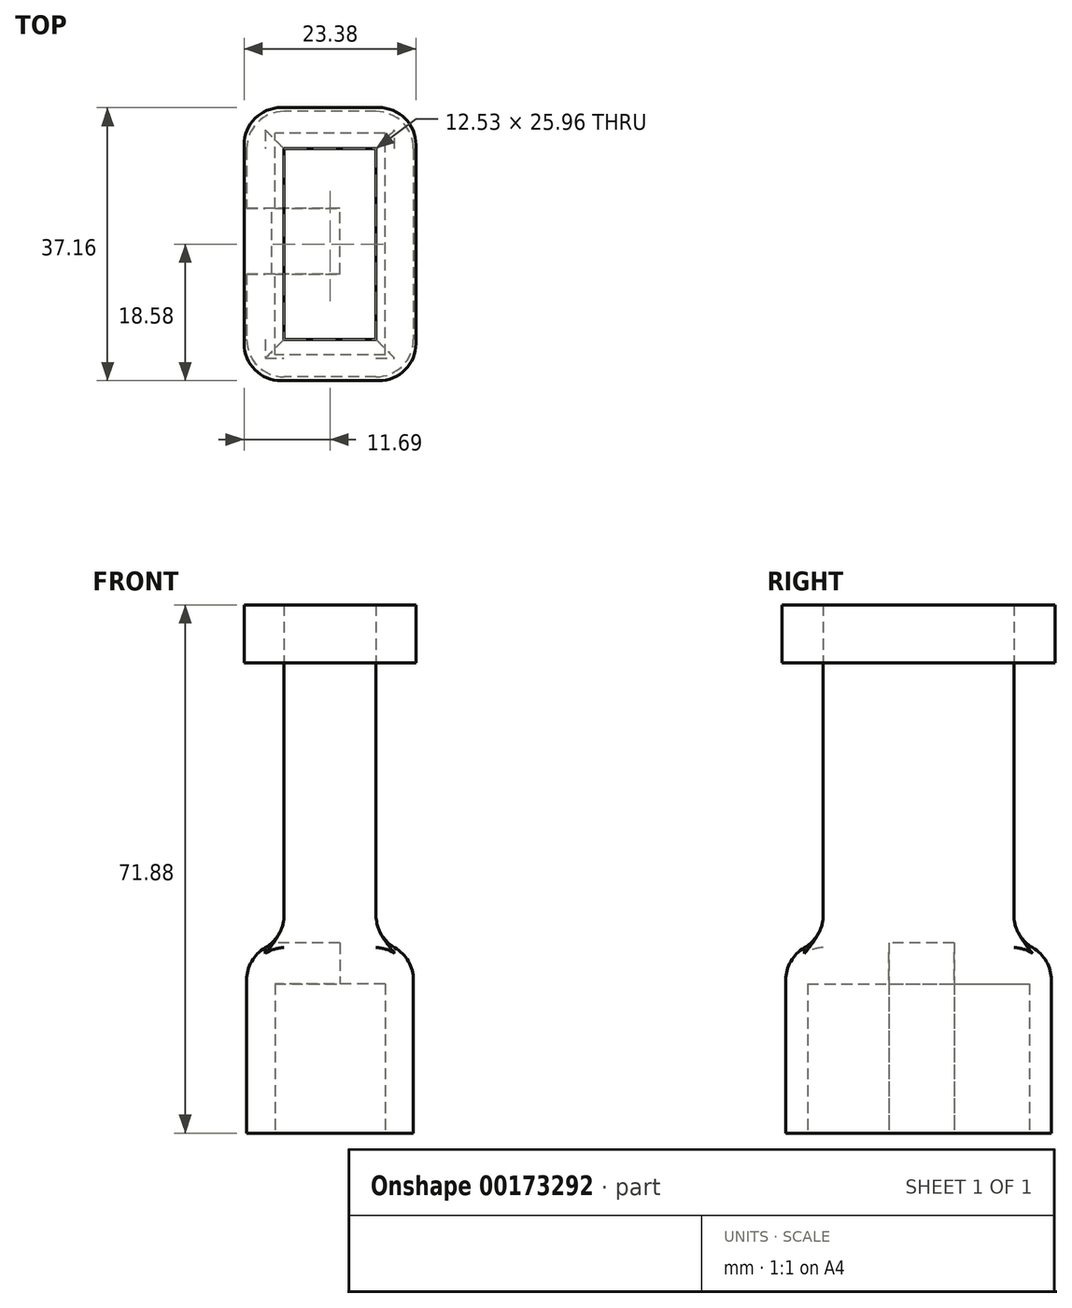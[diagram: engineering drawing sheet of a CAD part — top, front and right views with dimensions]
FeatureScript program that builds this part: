
annotation { "Feature Type Name" : "Feature", "Feature Type Description" : "" }
export const myFeature = defineFeature(function(context is Context, id is Id, definition is map)
    precondition{}
    {
        {
            var Q0;
            Q0=qCreatedBy(makeId("Top.planeOp"),FACE);
            var sketch = newSketch(context, id + "F0", { "sketchPlane" : qUnion([Q0])});
            skLineSegment(sketch, "E0.bottom", {"start": v(11.34, 18.06) * mm, "end": v(-11.34, 18.06) * mm});
            skLineSegment(sketch, "E0.top", {"start": v(11.34, -18.06) * mm, "end": v(-11.34, -18.06) * mm});
            skLineSegment(sketch, "E0.left", {"start": v(11.34, 18.06) * mm, "end": v(11.34, -18.06) * mm});
            skLineSegment(sketch, "E0.right", {"start": v(-11.34, 18.06) * mm, "end": v(-11.34, -18.06) * mm});
            skPoint(sketch, "E0.middle", {"position": v(0, 0) * mm});
            skSolve(sketch);
        }
        {
            var Q0;
            Q0=makeQuery(id+"F0.imprint","IMPRINT",FACE,{"disambiguationData":[TD([[makeQuery(id+"F0.imprint","IMPRINT",EDGE,{"derivedFrom":sQuery(id+"F0.wireOp",EDGE,"E0.bottom")}),1.0]])]});
            extrude(context, id + "F1", {"entities" : qUnion([Q0]), "depth" : 25.9 * mm});
        }
        {
            var Q0;
            Q0=makeQuery(id+"F1.opExtrude","CAP_EDGE",EDGE,{"disambiguationData":[OSD([sQuery(id+"F0.wireOp",EDGE,"E0.right")])],"isStart":false});
            var Q1;
            Q1=makeQuery(id+"F1.opExtrude","CAP_EDGE",EDGE,{"disambiguationData":[OSD([sQuery(id+"F0.wireOp",EDGE,"E0.bottom")])],"isStart":false});
            var Q2;
            Q2=makeQuery(id+"F1.opExtrude","SWEPT_EDGE",EDGE,{"disambiguationData":[OSD([sQuery(id+"F0.wireOp",EDGE,"E0.bottom"),sQuery(id+"F0.wireOp",EDGE,"E0.right")])]});
            var Q3;
            Q3=makeQuery(id+"F1.opExtrude","SWEPT_EDGE",EDGE,{"disambiguationData":[OSD([sQuery(id+"F0.wireOp",EDGE,"E0.bottom"),sQuery(id+"F0.wireOp",EDGE,"E0.left")])]});
            var Q4;
            Q4=makeQuery(id+"F1.opExtrude","CAP_EDGE",EDGE,{"disambiguationData":[OSD([sQuery(id+"F0.wireOp",EDGE,"E0.left")])],"isStart":false});
            var Q5;
            Q5=makeQuery(id+"F1.opExtrude","CAP_EDGE",EDGE,{"disambiguationData":[OSD([sQuery(id+"F0.wireOp",EDGE,"E0.top")])],"isStart":false});
            var Q6;
            Q6=makeQuery(id+"F1.opExtrude","SWEPT_EDGE",EDGE,{"disambiguationData":[OSD([sQuery(id+"F0.wireOp",EDGE,"E0.top"),sQuery(id+"F0.wireOp",EDGE,"E0.left")])]});
            var Q7;
            Q7=makeQuery(id+"F1.opExtrude","SWEPT_EDGE",EDGE,{"disambiguationData":[OSD([sQuery(id+"F0.wireOp",EDGE,"E0.top"),sQuery(id+"F0.wireOp",EDGE,"E0.right")])]});
            fillet(context, id + "F2", {"entities" : qUnion([Q0, Q1, Q2, Q3, Q4, Q5, Q6, Q7]), "radius" : 5.08 * mm, "tangentPropagation" : true, "allowEdgeOverflow" : false});
        }
        {
            var Q0;
            Q0=makeQuery(id+"F1.opExtrude","CAP_FACE",FACE,{"disambiguationData":[OSD([sQuery(id+"F0.wireOp",EDGE,"E0.bottom"),sQuery(id+"F0.wireOp",EDGE,"E0.top"),sQuery(id+"F0.wireOp",EDGE,"E0.left"),sQuery(id+"F0.wireOp",EDGE,"E0.right")])],"isStart":false});
            var sketch = newSketch(context, id + "F3", { "sketchPlane" : qUnion([Q0])});
            skLineSegment(sketch, "E1.bottom", {"start": v(6.26, 12.98) * mm, "end": v(-6.26, 12.98) * mm});
            skLineSegment(sketch, "E1.top", {"start": v(6.26, -12.98) * mm, "end": v(-6.26, -12.98) * mm});
            skLineSegment(sketch, "E1.left", {"start": v(6.26, 12.98) * mm, "end": v(6.26, -12.98) * mm});
            skLineSegment(sketch, "E1.right", {"start": v(-6.26, 12.98) * mm, "end": v(-6.26, -12.98) * mm});
            skPoint(sketch, "E1.middle", {"position": v(0, 0) * mm});
            skSolve(sketch);
        }
        {
            var Q0;
            Q0=makeQuery(id+"F3.imprint","IMPRINT",FACE,{"disambiguationData":[TD([[makeQuery(id+"F3.imprint","IMPRINT",EDGE,{"derivedFrom":sQuery(id+"F3.wireOp",EDGE,"E1.bottom")}),1.0]])]});
            extrude(context, id + "F4", {"entities" : qUnion([Q0]), "operationType" : NewBodyOperationType.ADD, "depth" : 38.1 * mm});
        }
        {
            var Q0;
            Q0=makeQuery(id+"F4.opExtrude","CAP_FACE",FACE,{"disambiguationData":[OSD([sQuery(id+"F3.wireOp",EDGE,"E1.bottom"),sQuery(id+"F3.wireOp",EDGE,"E1.top"),sQuery(id+"F3.wireOp",EDGE,"E1.left"),sQuery(id+"F3.wireOp",EDGE,"E1.right")])],"isStart":false});
            var sketch = newSketch(context, id + "F5", { "sketchPlane" : qUnion([Q0])});
            skLineSegment(sketch, "E2.bottom", {"start": v(11.7, 18.58) * mm, "end": v(-11.7, 18.58) * mm});
            skLineSegment(sketch, "E2.top", {"start": v(11.7, -18.58) * mm, "end": v(-11.7, -18.58) * mm});
            skLineSegment(sketch, "E2.left", {"start": v(11.7, 18.58) * mm, "end": v(11.7, -18.58) * mm});
            skLineSegment(sketch, "E2.right", {"start": v(-11.7, 18.58) * mm, "end": v(-11.7, -18.58) * mm});
            skPoint(sketch, "E2.middle", {"position": v(0, 0) * mm});
            skSolve(sketch);
        }
        {
            var Q0;
            Q0=makeQuery(id+"F5.imprint","IMPRINT",FACE,{"disambiguationData":[TD([[makeQuery(id+"F5.imprint","IMPRINT",EDGE,{"derivedFrom":sQuery(id+"F5.wireOp",EDGE,"E2.bottom")}),1.0]])]});
            extrude(context, id + "F6", {"entities" : qUnion([Q0]), "depth" : 7.87 * mm});
        }
        {
            var Q0;
            Q0=makeQuery(id+"F4.opExtrude","CAP_FACE",FACE,{"disambiguationData":[OSD([sQuery(id+"F3.wireOp",EDGE,"E1.bottom"),sQuery(id+"F3.wireOp",EDGE,"E1.top"),sQuery(id+"F3.wireOp",EDGE,"E1.left"),sQuery(id+"F3.wireOp",EDGE,"E1.right")])],"isStart":false});
            var Q1;
            Q1=makeQuery(id+"F6.opExtrude","CAP_FACE",FACE,{"disambiguationData":[OSD([sQuery(id+"F3.wireOp",EDGE,"E1.bottom"),sQuery(id+"F3.wireOp",EDGE,"E1.top"),sQuery(id+"F3.wireOp",EDGE,"E1.left"),sQuery(id+"F3.wireOp",EDGE,"E1.right"),sQuery(id+"F5.wireOp",EDGE,"E2.bottom"),sQuery(id+"F5.wireOp",EDGE,"E2.top"),sQuery(id+"F5.wireOp",EDGE,"E2.left"),sQuery(id+"F5.wireOp",EDGE,"E2.right")])],"isStart":false});
            extrude(context, id + "F7", {"entities" : qUnion([Q0]), "endBound" : BoundingType.UP_TO_SURFACE, "endBoundEntityFace" : qUnion([Q1]), "depth" : 7.37 * mm});
        }
        {
            var Q0;
            Q0=makeQuery(id+"F1.opExtrude","CAP_FACE",FACE,{"disambiguationData":[OSD([sQuery(id+"F0.wireOp",EDGE,"E0.bottom"),sQuery(id+"F0.wireOp",EDGE,"E0.top"),sQuery(id+"F0.wireOp",EDGE,"E0.left"),sQuery(id+"F0.wireOp",EDGE,"E0.right")])],"isStart":true});
            var sketch = newSketch(context, id + "F8", { "sketchPlane" : qUnion([Q0])});
            skLineSegment(sketch, "E3.bottom", {"start": v(7.5, 15.1) * mm, "end": v(-7.5, 15.1) * mm});
            skLineSegment(sketch, "E3.top", {"start": v(7.5, -15.1) * mm, "end": v(-7.5, -15.1) * mm});
            skLineSegment(sketch, "E3.left", {"start": v(7.5, 15.1) * mm, "end": v(7.5, -15.1) * mm});
            skLineSegment(sketch, "E3.right", {"start": v(-7.5, 15.1) * mm, "end": v(-7.5, -15.1) * mm});
            skPoint(sketch, "E3.middle", {"position": v(0, 0) * mm});
            skSolve(sketch);
        }
        {
            var Q0;
            Q0=makeQuery(id+"F8.imprint","IMPRINT",FACE,{"disambiguationData":[TD([[makeQuery(id+"F8.imprint","IMPRINT",EDGE,{"derivedFrom":sQuery(id+"F8.wireOp",EDGE,"E3.bottom")}),1.0]])]});
            extrude(context, id + "F9", {"entities" : qUnion([Q0]), "operationType" : NewBodyOperationType.REMOVE, "oppositeDirection" : true, "depth" : 20.32 * mm});
        }
        {
            var Q0;
            Q0=makeQuery(id+"F1.opExtrude","SWEPT_FACE",FACE,{"disambiguationData":[OSD([sQuery(id+"F0.wireOp",EDGE,"E0.right")])]});
            var sketch = newSketch(context, id + "F10", { "sketchPlane" : qUnion([Q0])});
            skLineSegment(sketch, "E4.bottom", {"start": v(-4.85, 25.88) * mm, "end": v(4.05, 25.88) * mm});
            skLineSegment(sketch, "E4.top", {"start": v(-4.85, 0) * mm, "end": v(4.05, 0) * mm});
            skLineSegment(sketch, "E4.left", {"start": v(-4.85, 25.88) * mm, "end": v(-4.85, 0) * mm});
            skLineSegment(sketch, "E4.right", {"start": v(4.05, 25.88) * mm, "end": v(4.05, 0) * mm});
            skSolve(sketch);
        }
        {
            var Q0;
            {var subQ0=sQuery(id+"F10.wireOp",EDGE,"E4.bottom");Q0=makeQuery(id+"F10.imprint","IMPRINT",FACE,{"disambiguationData":[TD([[makeQuery(id+"F10.imprint","IMPRINT",EDGE,{"derivedFrom":subQ0}),-1.0]])]});}
            var Q1;
            {var subQ0=sQuery(id+"F10.wireOp",EDGE,"E4.top");Q1=makeQuery(id+"F10.imprint","IMPRINT",FACE,{"disambiguationData":[TD([[makeQuery(id+"F10.imprint","IMPRINT",EDGE,{"derivedFrom":subQ0}),1.0]])]});}
            extrude(context, id + "F11", {"entities" : qUnion([Q0, Q1]), "operationType" : NewBodyOperationType.REMOVE, "oppositeDirection" : true, "depth" : 12.7 * mm});
        }
        {
            var Q0;
            Q0=makeQuery(id+"F6.opExtrude","SWEPT_EDGE",EDGE,{"disambiguationData":[OSD([sQuery(id+"F5.wireOp",EDGE,"E2.top"),sQuery(id+"F5.wireOp",EDGE,"E2.left")])]});
            var Q1;
            Q1=makeQuery(id+"F6.opExtrude","SWEPT_EDGE",EDGE,{"disambiguationData":[OSD([sQuery(id+"F5.wireOp",EDGE,"E2.top"),sQuery(id+"F5.wireOp",EDGE,"E2.right")])]});
            var Q2;
            Q2=makeQuery(id+"F6.opExtrude","SWEPT_EDGE",EDGE,{"disambiguationData":[OSD([sQuery(id+"F5.wireOp",EDGE,"E2.bottom"),sQuery(id+"F5.wireOp",EDGE,"E2.right")])]});
            var Q3;
            Q3=makeQuery(id+"F6.opExtrude","SWEPT_EDGE",EDGE,{"disambiguationData":[OSD([sQuery(id+"F5.wireOp",EDGE,"E2.bottom"),sQuery(id+"F5.wireOp",EDGE,"E2.left")])]});
            fillet(context, id + "F12", {"entities" : qUnion([Q0, Q1, Q2, Q3]), "radius" : 5.08 * mm, "tangentPropagation" : true, "allowEdgeOverflow" : false});
        }
        {
            var Q0;
            {var subQ0=sQuery(id+"F0.wireOp",EDGE,"E0.top");Q0=makeQuery(id+"F4.boolean.opBoolean","MERGE",EDGE,{"derivedFrom":[makeQuery(id+"F2.opFillet","BLEND_EDGE",EDGE,{"blendedFrom":[makeQuery(id+"F1.opExtrude","CAP_EDGE",EDGE,{"disambiguationData":[OSD([subQ0])],"isStart":false}),makeQuery(id+"F1.opExtrude","CAP_FACE",FACE,{"disambiguationData":[OSD([sQuery(id+"F0.wireOp",EDGE,"E0.bottom"),subQ0,sQuery(id+"F0.wireOp",EDGE,"E0.left"),sQuery(id+"F0.wireOp",EDGE,"E0.right")])],"isStart":false})],"blendedInto":[makeQuery(id+"F1.opExtrude","CAP_FACE",FACE,{"disambiguationData":[OSD([sQuery(id+"F0.wireOp",EDGE,"E0.bottom"),subQ0,sQuery(id+"F0.wireOp",EDGE,"E0.left"),sQuery(id+"F0.wireOp",EDGE,"E0.right")])],"isStart":false})]}),makeQuery(id+"F4.opExtrude","CAP_EDGE",EDGE,{"disambiguationData":[OSD([sQuery(id+"F3.wireOp",EDGE,"E1.top")])],"isStart":true})]});}
            var Q1;
            {var subQ0=sQuery(id+"F0.wireOp",EDGE,"E0.right");Q1=makeQuery(id+"F4.boolean.opBoolean","MERGE",EDGE,{"derivedFrom":[makeQuery(id+"F2.opFillet","BLEND_EDGE",EDGE,{"blendedFrom":[makeQuery(id+"F1.opExtrude","CAP_EDGE",EDGE,{"disambiguationData":[OSD([subQ0])],"isStart":false}),makeQuery(id+"F1.opExtrude","CAP_FACE",FACE,{"disambiguationData":[OSD([sQuery(id+"F0.wireOp",EDGE,"E0.bottom"),sQuery(id+"F0.wireOp",EDGE,"E0.top"),sQuery(id+"F0.wireOp",EDGE,"E0.left"),subQ0])],"isStart":false})],"blendedInto":[makeQuery(id+"F1.opExtrude","CAP_FACE",FACE,{"disambiguationData":[OSD([sQuery(id+"F0.wireOp",EDGE,"E0.bottom"),sQuery(id+"F0.wireOp",EDGE,"E0.top"),sQuery(id+"F0.wireOp",EDGE,"E0.left"),subQ0])],"isStart":false})]}),makeQuery(id+"F4.opExtrude","CAP_EDGE",EDGE,{"disambiguationData":[OSD([sQuery(id+"F3.wireOp",EDGE,"E1.right")])],"isStart":true})]});}
            var Q2;
            {var subQ0=sQuery(id+"F0.wireOp",EDGE,"E0.bottom");Q2=makeQuery(id+"F4.boolean.opBoolean","MERGE",EDGE,{"derivedFrom":[makeQuery(id+"F2.opFillet","BLEND_EDGE",EDGE,{"blendedFrom":[makeQuery(id+"F1.opExtrude","CAP_EDGE",EDGE,{"disambiguationData":[OSD([subQ0])],"isStart":false}),makeQuery(id+"F1.opExtrude","CAP_FACE",FACE,{"disambiguationData":[OSD([subQ0,sQuery(id+"F0.wireOp",EDGE,"E0.top"),sQuery(id+"F0.wireOp",EDGE,"E0.left"),sQuery(id+"F0.wireOp",EDGE,"E0.right")])],"isStart":false})],"blendedInto":[makeQuery(id+"F1.opExtrude","CAP_FACE",FACE,{"disambiguationData":[OSD([subQ0,sQuery(id+"F0.wireOp",EDGE,"E0.top"),sQuery(id+"F0.wireOp",EDGE,"E0.left"),sQuery(id+"F0.wireOp",EDGE,"E0.right")])],"isStart":false})]}),makeQuery(id+"F4.opExtrude","CAP_EDGE",EDGE,{"disambiguationData":[OSD([sQuery(id+"F3.wireOp",EDGE,"E1.bottom")])],"isStart":true})]});}
            var Q3;
            {var subQ0=sQuery(id+"F0.wireOp",EDGE,"E0.left");Q3=makeQuery(id+"F4.boolean.opBoolean","MERGE",EDGE,{"derivedFrom":[makeQuery(id+"F2.opFillet","BLEND_EDGE",EDGE,{"blendedFrom":[makeQuery(id+"F1.opExtrude","CAP_EDGE",EDGE,{"disambiguationData":[OSD([subQ0])],"isStart":false}),makeQuery(id+"F1.opExtrude","CAP_FACE",FACE,{"disambiguationData":[OSD([sQuery(id+"F0.wireOp",EDGE,"E0.bottom"),sQuery(id+"F0.wireOp",EDGE,"E0.top"),subQ0,sQuery(id+"F0.wireOp",EDGE,"E0.right")])],"isStart":false})],"blendedInto":[makeQuery(id+"F1.opExtrude","CAP_FACE",FACE,{"disambiguationData":[OSD([sQuery(id+"F0.wireOp",EDGE,"E0.bottom"),sQuery(id+"F0.wireOp",EDGE,"E0.top"),subQ0,sQuery(id+"F0.wireOp",EDGE,"E0.right")])],"isStart":false})]}),makeQuery(id+"F4.opExtrude","CAP_EDGE",EDGE,{"disambiguationData":[OSD([sQuery(id+"F3.wireOp",EDGE,"E1.left")])],"isStart":true})]});}
            fillet(context, id + "F13", {"entities" : qUnion([Q0, Q1, Q2, Q3]), "radius" : 5.08 * mm, "tangentPropagation" : true, "allowEdgeOverflow" : false});
        }
    });
